# Revit family: Wall_Panel-Teknion-CWVH-Chronicle-TV_Wall_Panel-R2022
name_source: partatom
category: Furniture
units: mm (PartAtom-declared; Revit-internal decimal feet)

## family parameters
Always vertical = Yes
Cut with Voids When Loaded = No
OmniClass Number = 23.40.20.00
OmniClass Title = General Furniture and Specialties
Render Appearance Source = Family Geometry
Room Calculation Point = No
Shared = Yes
Work Plane-Based = No

## types (4) — shared parameters
Assembly Code = E2020200
Description = Chronicle - TV Wall Panel
Manufacturer = Teknion
Manufacturer Fax = 416.661.4586
Part Number = CWVH
Product Documentation Link = https://www.teknion.com
Product Line = TV Wall Panel
Product Page URL = https://www.teknion.com
Series = Chronicle
Sustainability Data = https://www.teknion.com
URL = www.teknion.com
Unit Weight URL = http://www.teknion.com
Warranty = http://www.teknion.com
zero-valued in all types: Default Elevation

## per-type parameters (varying)
| type | 2H | 3H | 4H | Height | Model |
| (2H) 2 High, 26.5" | Yes | No | No | 26.5 " | CWVH2HF__ |
| (3H) 3 High, 41.25" | No | Yes | No | 41.25 " | CWVH3HF__ |
| (4H) 4 High, 55" | No | No | Yes | 55 " | CWVH4HF__ |
| (3H) 3 High, 40.25" (Height Reduced by 1") | No | No | No | 40.25 " | CWVH3HR__ |

## geometry (parser evidence)
native form markers: Sweep x3
no freeform markers — native parametric forms only
